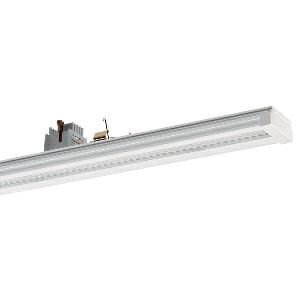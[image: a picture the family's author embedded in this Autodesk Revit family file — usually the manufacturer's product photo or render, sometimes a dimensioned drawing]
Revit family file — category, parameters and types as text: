
# Revit family: conveo_-_cvg_4500_850_xn-l_ea_5_226848449-00804983_689a
name_source: partatom
category: Lighting Fixtures
units: mm (PartAtom-declared; Revit-internal decimal feet)

## family parameters
Cut with Voids When Loaded = No
Host = Face
Light Source = No
Part Type = Normal
Room Calculation Point = No
Round Connector Dimension = Use Diameter
Shared = No

## types (1)
- CONVEO - CVG 4500/850/xN-L/EA/5 (1 x LED, 4650 lm, 5000K)
    Apparent Load = 27 VA
    Approval mark = CE
    CIE Flux Codes = 84 95 99 100 100
    Color Rendering = 80-89
    Color Temperature = 5000K
    Control Gear = Electronic ballast
    Default Elevation = 1800 mm
    Description = CVG 4500/850/xN-L/EA/5|Continuous-row system|light source: LED|work equipment: Electronic ballast|connected load: 220-240 V, 50-60 Hz|Power consumption: approx. 27 W|luminous flux: 4650 lm|luminous efficacy: 172 lm/W|colour temperature: Cold white, ca. 5000 K|color rendering index (CRI): >= 80|chromaticity tolerance:  3 SDCM|System of protection: IP 54|class of protection: I|technology: Switchable|luminaire body|material: Aluminium|surface: Powder coatet|colour: White|lamp cover: Acrylic (PMMA), Satine|weight (net): approx. 1.9 kg|Fastening: Available separately|maximum ambient temperature: 50 ░C|glare control: Lens optics|Approval mark: VDE - ENEC|
    Frequency = 50 Hz
    Height = 70 mm
    Lamp = 1 x LED
    Lamp Light Flux = 4650 lm
    Lamp count = 1
    Length = 1500 mm
    Luminous efficacy = 172 lm/W
    Manufacturer = Waldmann
    ModVariant = No
    Model = 226848449-00804983
    Mounting Place = Ceiling
    Mounting Type = Pendant
    Number of Poles = 1
    OnlyDefault = Yes
    Power Factor = 1
    Product Name = CONVEO - CVG 4500/850/xN-L/EA/5
    Product group = Continuous-row system (industry)
    ProductGroupID = 301
    Protection Class = Protection class I
    Protection Degree = IP 54
    RLX_Detail_Level = 1
    RlxData = <blob elided: 100781 chars, md5=0c0dd0c6>
    Socket = socket
    Standby Power = 0 W
    System Light Flux = 4650 lm
    System Power = 27 W
    Type Comments = Product without accessories
    Type Image = 226848319-00804970_1l5.jpg
    URL = http://relux.com
    VarID = ---
    Voltage = 230 V
    Voltage Range = 220-240 V
    Weight = 0.00 kg
    Width = 64 mm

## geometry (parser evidence)
native form markers: Blend x4, Sweep x8
no freeform markers — native parametric forms only
